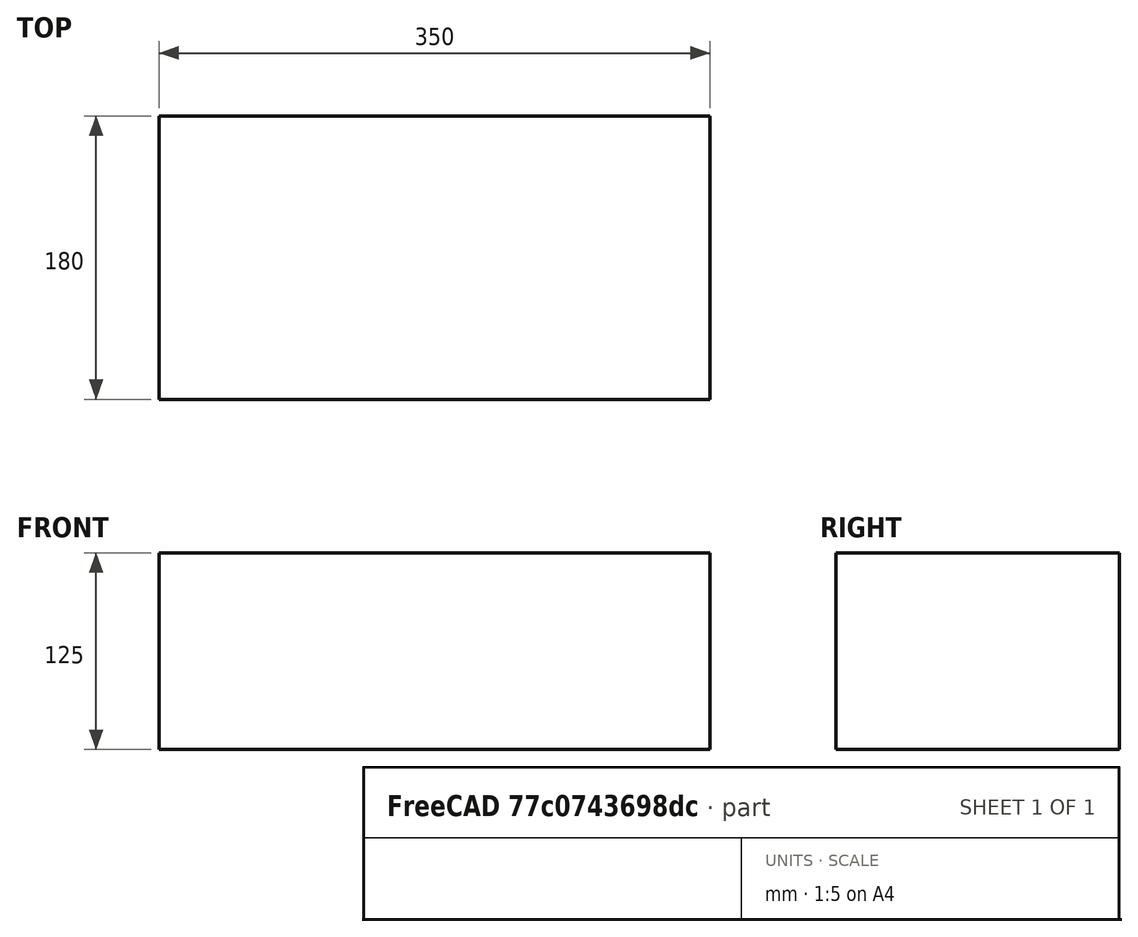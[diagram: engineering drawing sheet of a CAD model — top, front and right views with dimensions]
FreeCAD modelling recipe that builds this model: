
FCSTD DOCUMENT  (FreeCAD 1.0R39109 (Git))
Label: Monochromator
License: All rights reserved
LicenseURL: https://en.wikipedia.org/wiki/All_rights_reserved
objects: PartDesign::CoordinateSystem×2, App::DocumentObjectGroup×2, Sketcher::SketchObject×1, PartDesign::Pad×1, PartDesign::Body×1, App::FeaturePython×1, App::Part×1
note: 8 computed .brp shape members not serialized (recipe doc carries the construction recipe); baked Part::Feature solids carry a one-line shape summary decoded from their .brp

FEATURE [Sketcher::SketchObject] Sketch
  ArcFitTolerance = 1e-06
  AttachmentSupport = -> [XY_Plane]
  FullyConstrained = true
  MakeInternals = false
  MapMode = 5
  sketch-geometry (4):
    g0: LineSegment StartX=-175 StartY=90 StartZ=0 EndX=-175 EndY=-90 EndZ=0
    g1: LineSegment StartX=-175 StartY=-90 StartZ=0 EndX=175 EndY=-90 EndZ=0
    g2: LineSegment StartX=175 StartY=-90 StartZ=0 EndX=175 EndY=90 EndZ=0
    g3: LineSegment StartX=175 StartY=90 StartZ=0 EndX=-175 EndY=90 EndZ=0
  constraints (12):
    c: Coincident(g0,g1)
    c: Coincident(g1,g2)
    c: Coincident(g2,g3)
    c: Coincident(g3,g0)
    c: Vertical(g0)
    c: Vertical(g2)
    c: Horizontal(g1)
    c: Horizontal(g3)
    c: DistanceX(g3,g3) = 350
    c: DistanceY(g0,g0) = 180
    c: DistanceX(g0,g-1) = 175
    c: DistanceY(g-1,g2) = 90
FEATURE [PartDesign::Pad] Pad
  Direction = (0,0,1)
  Length = 125
  Length2 = 10
  Profile = -> Sketch
  ReferenceAxis = -> Sketch [N_Axis]
  Suppressed = false
  Type = 0
FEATURE [PartDesign::Body] Body
  AllowCompound = false
  Group = -> [Sketch,Pad]
  Origin = -> Origin
  Tip = -> Pad
FEATURE [PartDesign::CoordinateSystem] LCS_Origin
  AttacherType = Attacher::AttachEngine3D
  AttachmentSupport = -> [X_Axis001]
  MapMode = 2
FEATURE [App::DocumentObjectGroup] Constraints
FEATURE [App::FeaturePython] Variables  # WARN: FeaturePython — macro-defined, semantics opaque (R4)
  Type = App::PropertyContainer
FEATURE [App::DocumentObjectGroup] Configurations
FEATURE [PartDesign::CoordinateSystem] LCS_1  label="BottomCorner"
  AttacherType = Attacher::AttachEngine3D
  Placement = pos=(-175,-100,0) rot=(0,0,1;0rad)
FEATURE [App::Part] Assembly
  AssemblyType = Part::Link
  Group = -> [LCS_Origin,Constraints,Variables,Configurations,Body,LCS_1]
  Origin = -> Origin001
  Type = Assembly
